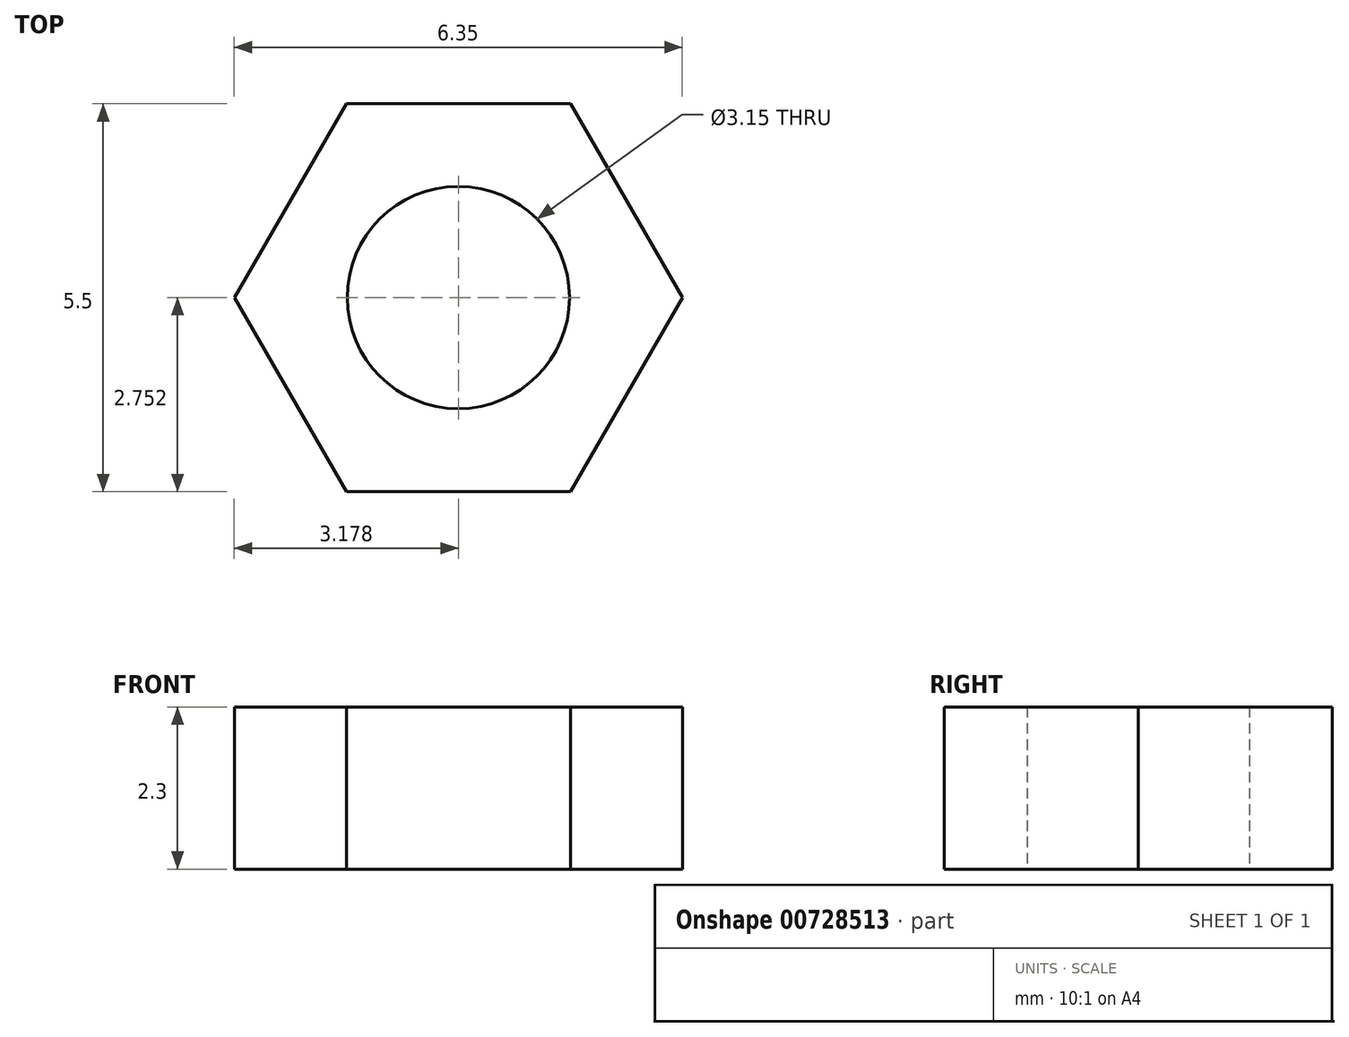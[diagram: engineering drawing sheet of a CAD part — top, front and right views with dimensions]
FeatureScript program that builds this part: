
annotation { "Feature Type Name" : "Feature", "Feature Type Description" : "" }
export const myFeature = defineFeature(function(context is Context, id is Id, definition is map)
    precondition{}
    {
        {
            var Q0;
            Q0=qCreatedBy(makeId("Top.planeOp"),FACE);
            var sketch = newSketch(context, id + "F0", { "sketchPlane" : qUnion([Q0])});
            skCircle(sketch, "E0.cCircle", {"center": v(-1.16, 1.16) * mm, "radius": 3.18 * mm, "construction": true});
            skLineSegment(sketch, "E0.0", {"start": v(0.43, 3.91) * mm, "end": v(2.01, 1.16) * mm});
            skLineSegment(sketch, "E0.1", {"start": v(2.01, 1.16) * mm, "end": v(0.43, -1.59) * mm});
            skLineSegment(sketch, "E0.2", {"start": v(0.43, -1.59) * mm, "end": v(-2.75, -1.59) * mm});
            skLineSegment(sketch, "E0.3", {"start": v(-2.75, -1.59) * mm, "end": v(-4.34, 1.16) * mm});
            skLineSegment(sketch, "E0.4", {"start": v(-4.34, 1.16) * mm, "end": v(-2.75, 3.91) * mm});
            skLineSegment(sketch, "E0.5", {"start": v(-2.75, 3.91) * mm, "end": v(0.43, 3.91) * mm});
            skSolve(sketch);
        }
        {
            var Q0;
            Q0 = qSketchRegion(id + "F0", true);
            extrude(context, id + "F1", {"entities" : qUnion([Q0]), "depth" : (3.9 - 1.6) * mm, "offsetDistance" : 25 * mm});
        }
        {
            var Q0;
            Q0=sQuery(id+"F0.wireOp",VERTEX,"E0.cCircle.center");
            var Q1;
            Q1=makeQuery(id+"F1.opExtrude","SWEPT_BODY",BODY,{"disambiguationData":[OSD([sQuery(id+"F0.wireOp",EDGE,"E0.0"),sQuery(id+"F0.wireOp",EDGE,"E0.1"),sQuery(id+"F0.wireOp",EDGE,"E0.2"),sQuery(id+"F0.wireOp",EDGE,"E0.3"),sQuery(id+"F0.wireOp",EDGE,"E0.4"),sQuery(id+"F0.wireOp",EDGE,"E0.5")])]});
            hole(context, id + "F2", {"style" : HoleStyle.SIMPLE, "endStyle" : HoleEndStyle.THROUGH, "oppositeDirection" : true, "standardTappedOrClearance" : lookupTablePath({ "standard" : "ISO", "fit" : "Close", "size" : "M3", "type" : "Clearance" }), "standardBlindInLast" : lookupTablePath({ "fit" : "Close", "standard" : "ISO", "size" : "M3", "type" : "Clearance" }), "holeDiameter" : 3.15 * mm, "majorDiameter" : 5 * mm, "isTappedThrough" : true, "tappedDepth" : 12 * mm, "tapClearance" : 3, "locations" : qUnion([Q0]), "scope" : qUnion([Q1])});
        }
    });
